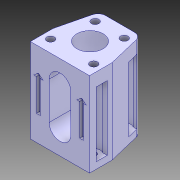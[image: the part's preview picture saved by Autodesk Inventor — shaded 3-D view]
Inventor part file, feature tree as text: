
AUTODESK INVENTOR PART (.ipt)
format: ipt  version: 2018 (Build 220112000, 112)  size: 408,576 bytes
history: native  units: mm
features: other x12, extrude x5, sketch x4
ambient origin geometry x8: Origin, YZ Plane, XZ Plane, XY Plane, X Axis, Y Axis, Z Axis, Center Point
bodies: Body1 (feature_tree)
feature tree (21):
  other  "Sólido1"
  extrude  "Extrusión1"  Depth=3.0mm
  other  "Edición directa3"
  other  "Edición directa4"
  extrude  "Extrusión2"  Depth=3.0mm
  extrude  "Extrusión3"  TaperAngle=0.0deg  [1 undecoded]
  other  "Edición directa8"
  other  "Edición directa11"
  extrude  "Extrusión14"  TaperAngle=0.0deg  [1 undecoded]
  extrude  "Extrusión15"  TaperAngle=0.0deg  [1 undecoded]
  sketch  "Boceto1"  dims[d6=3.0mm d7=3.0mm]
  sketch  "Boceto2"  dims[d8=3.0mm d9=3.0mm]
  sketch  "Boceto16"  dims[d10=3.0mm d11=0.0mm d15=0.0mm d16=0.0mm d17=-2.5mm]
  sketch  "Boceto17"  dims[d18=0.0mm d19=0.0mm d20=-2.5mm d21=0.0mm d22=0.0mm d23=-1.5mm d24=0.0mm d25=0.0mm d26=-2.0mm d27=7.0mm d28=7.0mm d29=7.0mm d30=7.0mm d31=7.0mm d32=0.0mm d33=1.0mm d34=1.0mm d35=4.0mm d36=3.0mm d37=1.5mm d39=1.5mm d40=1.5mm d41=0.0mm d97=0.0mm d98=0.0mm d99=10.0mm d108=0.0mm d109=0.0mm d110=10.0mm d111=15.0mm d112=90.0deg d113=15.0mm d114=9.5mm d115=0.0mm d120=4.2mm d121=4.2mm d123=10.0mm d126=10.0mm d127=11.0mm d128=0.0mm]
  other  "PartBody"
  other  "Desplazar4"
  other  "Desplazar5"
  other  "Desplazar6"
  other  "Desplazar7"
  other  "Desplazar13"
  other  "Desplazar16"
note: 3 required parameter values undecoded (feature->parameter linkage not recoverable at this tier; creation-order binding heuristic only, values carry confidence <= 0.55)
